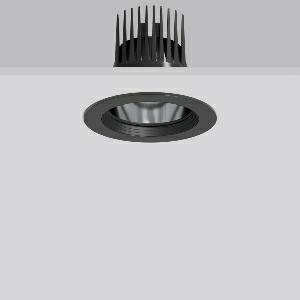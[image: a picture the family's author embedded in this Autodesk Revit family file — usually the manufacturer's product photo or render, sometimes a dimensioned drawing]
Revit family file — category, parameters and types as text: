
# Revit family: heledon_maxi_e_901784_003_2_f782
name_source: partatom
category: Lighting Fixtures
units: mm (PartAtom-declared; Revit-internal decimal feet)

## family parameters
Cut with Voids When Loaded = No
Host = Face
Light Source = No
Part Type = Normal
Room Calculation Point = No
Round Connector Dimension = Use Diameter
Shared = No

## types (1)
- HELEDON maxi E (1 x LED Modul 927 bakery, 3300 lm, 2700)
    Apparent Load = 33 VA
    Approval mark = CE
    CIE Flux Codes = 100 100 100 100 100
    Color Rendering = 90
    Color Temperature = 2700
    Default Elevation = 1800 mm
    Description = Series: HELEDON maxi
Round recessed downlight. Housing: die-cast aluminium, powder-coated. Black plastic ring and recessed LED to prevent glare from the side. Optical assembly with reflector made of MIRO-Silver with 98% total light reflection for outstanding efficiency - can be changed without tools. Special LED for illumination of pastries included. Suitable for Recessed ceiling mounting. Installation without tools thanks to spring fastening system. Including separate LED converter with connecting cable 600 mm.High quality converter without flickering and stroboscopic effect. Through-wiring box (5 pole) available as accessory. The following accessories can be mounted without use of tools: interchangeable lenses, decorative glasses, honeycomb louvre, clear and frosted diffusers, white interchangeable plastic ring. 
Colour: deep black, matt (RAL 9005)
Diameter: 162 mm
Height: 3 mm
Cut-out diameter: 152 mm
Recess height: 200 mm
Luminaire: recess height: 135 mm
Lamp: LED
Socket: without socket
Colour temperature: bakery
Colour rendering index (CRI): 97
System power: 33 W
Rated luminous flux: 3300 lm
Luminous efficiency: 100 lm/W
Control gear: Regulated power supply
Protection class: II
Type of protection: IP 20
    Height = 0 mm  [stored 0 ft]
    Lamp = 1 x LED Modul 927 bakery
    Lamp Light Flux = 3300 lm
    Lamp count = 1
    Length = 162 mm
    Lifetime = 50000 h
    Luminous efficacy = 100 lm/W
    Manufacturer = RZB
    ModVariant = No
    Model = 901784.003.2
    Mounting Place = Ceiling
    Mounting Type = Recessed
    Number of Poles = 1
    OnlyDefault = Yes
    Power Factor = 1
    Product Name = HELEDON maxi E
    Product group = Recessed downlights
    ProductGroupID = 402
    Protection Class = Protection class II
    Protection Degree = IP 20
    RLX_Detail_Level = 1
    RLX_Emergency_Light_Flux = 0 lm
    RLX_Emergency_Type = 0
    RLX_Emergency_Type_DB = No
    RlxData = <blob elided: 121897 chars, md5=468bda14>
    Socket = socket
    Standby Power = 0 W
    System Light Flux = 3300 lm
    System Power = 33 W
    Type Comments = Product without accessories
    Type Image = 901662.003.jpg
    URL = http://relux.com
    VarID = ---
    Voltage = 230 V
    Voltage Range = 220-240 V
    Weight = 0.00 kg
    Width = 0 mm  [stored 0 ft]

note: [stored X ft] marks values corroborated as IEEE doubles in the binary element streams (Revit-internal decimal feet)

## geometry (parser evidence)
native form markers: Blend x4, Sweep x12
no freeform markers — native parametric forms only
